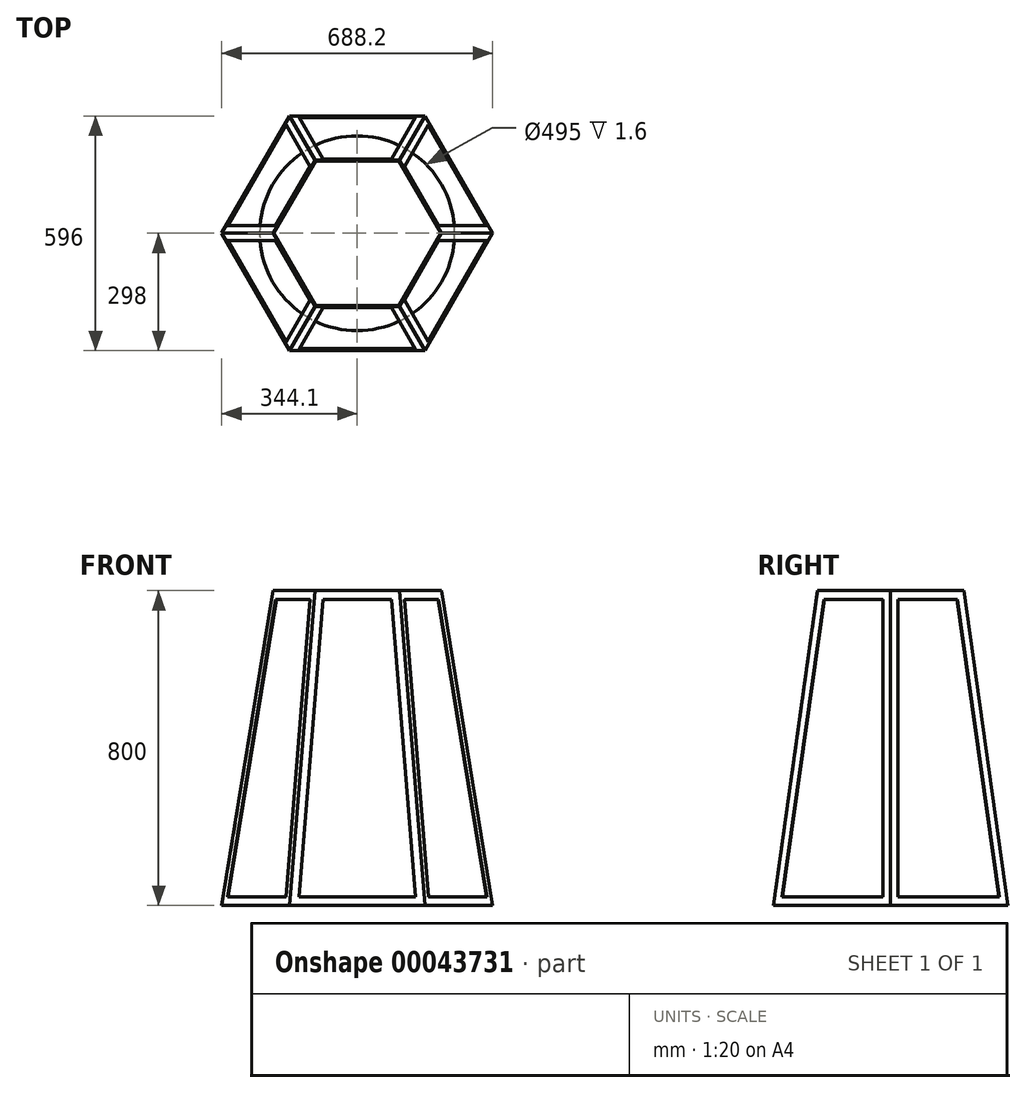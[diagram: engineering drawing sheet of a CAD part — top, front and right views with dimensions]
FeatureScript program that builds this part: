
annotation { "Feature Type Name" : "Feature", "Feature Type Description" : "" }
export const myFeature = defineFeature(function(context is Context, id is Id, definition is map)
    precondition{}
    {
        {
            var Q0;
            Q0=qCreatedBy(makeId("Top.planeOp"),FACE);
            var sketch = newSketch(context, id + "F0", { "sketchPlane" : qUnion([Q0])});
            skCircle(sketch, "E0.cCircle", {"center": v(0, 0) * mm, "radius": 298 * mm, "construction": true});
            skLineSegment(sketch, "E0.0", {"start": v(-172.05, 298) * mm, "end": v(172.05, 298) * mm});
            skLineSegment(sketch, "E0.1", {"start": v(172.05, 298) * mm, "end": v(344.1, 0) * mm});
            skLineSegment(sketch, "E0.2", {"start": v(344.1, 0) * mm, "end": v(172.05, -298) * mm});
            skLineSegment(sketch, "E0.3", {"start": v(172.05, -298) * mm, "end": v(-172.05, -298) * mm});
            skLineSegment(sketch, "E0.4", {"start": v(-172.05, -298) * mm, "end": v(-344.1, 0) * mm});
            skLineSegment(sketch, "E0.5", {"start": v(-344.1, 0) * mm, "end": v(-172.05, 298) * mm});
            skPoint(sketch, "E0.0.midPoint", {"position": v(0, 298) * mm});
            skSolve(sketch);
        }
        {
            var Q0;
            Q0=makeQuery(id+"F0.imprint","IMPRINT",FACE,{"disambiguationData":[TD([[makeQuery(id+"F0.imprint","IMPRINT",EDGE,{"derivedFrom":sQuery(id+"F0.wireOp",EDGE,"E0.0")}),-1.0]])]});
            extrude(context, id + "F1", {"entities" : qUnion([Q0]), "depth" : 800 * mm, "hasDraft" : true, "draftAngle" : 8 * degree, "draftPullDirection" : true});
        }
        {
            var Q0;
            Q0=makeQuery(id+"F1.opExtrude","CAP_FACE",FACE,{"disambiguationData":[OSD([sQuery(id+"F0.wireOp",EDGE,"E0.0"),sQuery(id+"F0.wireOp",EDGE,"E0.1"),sQuery(id+"F0.wireOp",EDGE,"E0.2"),sQuery(id+"F0.wireOp",EDGE,"E0.3"),sQuery(id+"F0.wireOp",EDGE,"E0.4"),sQuery(id+"F0.wireOp",EDGE,"E0.5")])],"isStart":false});
            shell(context, id + "F2", {"entities" : qUnion([Q0]), "thickness" : 1.6 * mm});
        }
        {
            var Q0;
            Q0=makeQuery(id+"F0.imprint","IMPRINT",FACE,{"disambiguationData":[TD([[makeQuery(id+"F0.imprint","IMPRINT",EDGE,{"derivedFrom":sQuery(id+"F0.wireOp",EDGE,"E0.0")}),-1.0]])]});
            var sketch = newSketch(context, id + "F3", { "sketchPlane" : qUnion([Q0])});
            skCircle(sketch, "E1", {"center": v(0, 0) * mm, "radius": 247.5 * mm});
            skSolve(sketch);
        }
        {
            var Q0;
            Q0 = qSketchRegion(id + "F3", true);
            extrude(context, id + "F4", {"entities" : qUnion([Q0]), "operationType" : NewBodyOperationType.REMOVE, "depth" : 25 * mm});
        }
        {
            var Q0;
            Q0=makeQuery(id+"F1.opExtrude","SWEPT_FACE",FACE,{"disambiguationData":[OSD([sQuery(id+"F0.wireOp",EDGE,"E0.3")])]});
            var sketch = newSketch(context, id + "F5", { "sketchPlane" : qUnion([Q0])});
            skLineSegment(sketch, "E2", {"start": v(-172.05, -41.47) * mm, "end": v(-107.14, 766.39) * mm});
            skLineSegment(sketch, "E3", {"start": v(-107.14, 766.39) * mm, "end": v(107.14, 766.39) * mm});
            skLineSegment(sketch, "E4", {"start": v(107.14, 766.39) * mm, "end": v(172.05, -41.47) * mm});
            skLineSegment(sketch, "E5", {"start": v(172.05, -41.47) * mm, "end": v(-172.05, -41.47) * mm});
            skLineSegment(sketch, "E6.0", {"start": v(-148.21, -19.47) * mm, "end": v(148.21, -19.47) * mm});
            skLineSegment(sketch, "E6.1", {"start": v(-86.83, 744.39) * mm, "end": v(-148.21, -19.47) * mm});
            skLineSegment(sketch, "E6.2", {"start": v(86.83, 744.39) * mm, "end": v(-86.83, 744.39) * mm});
            skLineSegment(sketch, "E6.3", {"start": v(148.21, -19.47) * mm, "end": v(86.83, 744.39) * mm});
            skSolve(sketch);
        }
        {
            var Q0;
            Q0=makeQuery(id+"F5.imprint","IMPRINT",FACE,{"disambiguationData":[TD([[makeQuery(id+"F5.imprint","IMPRINT",EDGE,{"derivedFrom":sQuery(id+"F5.wireOp",EDGE,"E6.0")}),1.0]])]});
            extrude(context, id + "F6", {"entities" : qUnion([Q0]), "operationType" : NewBodyOperationType.REMOVE, "oppositeDirection" : true, "depth" : 25 * mm});
        }
        {
            var Q0;
            Q0=makeQuery(id+"F1.opExtrude","SWEPT_FACE",FACE,{"disambiguationData":[OSD([sQuery(id+"F0.wireOp",EDGE,"E0.4")])]});
            var sketch = newSketch(context, id + "F7", { "sketchPlane" : qUnion([Q0])});
            skLineSegment(sketch, "E7", {"start": v(-168.18, -55.12) * mm, "end": v(174.82, -27.56) * mm});
            skLineSegment(sketch, "E8", {"start": v(174.82, -27.56) * mm, "end": v(45.41, 772.5) * mm});
            skLineSegment(sketch, "E9", {"start": v(45.41, 772.5) * mm, "end": v(-168.18, 755.35) * mm});
            skLineSegment(sketch, "E10", {"start": v(-168.18, 755.35) * mm, "end": v(-168.18, -55.12) * mm});
            skLineSegment(sketch, "E11.0", {"start": v(-146.18, -31.28) * mm, "end": v(149.3, -7.54) * mm});
            skLineSegment(sketch, "E11.1", {"start": v(-146.18, 735.04) * mm, "end": v(-146.18, -31.28) * mm});
            skLineSegment(sketch, "E11.2", {"start": v(26.93, 748.95) * mm, "end": v(-146.18, 735.04) * mm});
            skLineSegment(sketch, "E11.3", {"start": v(149.3, -7.54) * mm, "end": v(26.93, 748.95) * mm});
            skSolve(sketch);
        }
        {
            var Q0;
            Q0=makeQuery(id+"F7.imprint","IMPRINT",FACE,{"disambiguationData":[TD([[makeQuery(id+"F7.imprint","IMPRINT",EDGE,{"derivedFrom":sQuery(id+"F7.wireOp",EDGE,"E11.0")}),1.0]])]});
            extrude(context, id + "F8", {"entities" : qUnion([Q0]), "operationType" : NewBodyOperationType.REMOVE, "oppositeDirection" : true, "depth" : 25 * mm});
        }
        {
            var Q0;
            Q0=makeQuery(id+"F1.opExtrude","SWEPT_FACE",FACE,{"disambiguationData":[OSD([sQuery(id+"F0.wireOp",EDGE,"E0.5")])]});
            var sketch = newSketch(context, id + "F9", { "sketchPlane" : qUnion([Q0])});
            skLineSegment(sketch, "E12", {"start": v(-45.41, 772.5) * mm, "end": v(168.18, 755.35) * mm});
            skLineSegment(sketch, "E13", {"start": v(168.18, 755.35) * mm, "end": v(168.18, -55.12) * mm});
            skLineSegment(sketch, "E14", {"start": v(168.18, -55.12) * mm, "end": v(-174.82, -27.56) * mm});
            skLineSegment(sketch, "E15", {"start": v(-174.82, -27.56) * mm, "end": v(-45.41, 772.5) * mm});
            skLineSegment(sketch, "E16.0", {"start": v(-26.93, 748.95) * mm, "end": v(146.18, 735.04) * mm});
            skLineSegment(sketch, "E16.1", {"start": v(-149.3, -7.54) * mm, "end": v(-26.93, 748.95) * mm});
            skLineSegment(sketch, "E16.2", {"start": v(146.18, -31.28) * mm, "end": v(-149.3, -7.54) * mm});
            skLineSegment(sketch, "E16.3", {"start": v(146.18, 735.04) * mm, "end": v(146.18, -31.28) * mm});
            skSolve(sketch);
        }
        {
            var Q0;
            Q0=makeQuery(id+"F9.imprint","IMPRINT",FACE,{"disambiguationData":[TD([[makeQuery(id+"F9.imprint","IMPRINT",EDGE,{"derivedFrom":sQuery(id+"F9.wireOp",EDGE,"E16.0")}),-1.0]])]});
            extrude(context, id + "F10", {"entities" : qUnion([Q0]), "operationType" : NewBodyOperationType.REMOVE, "oppositeDirection" : true, "depth" : 25 * mm});
        }
        {
            var Q0;
            Q0=makeQuery(id+"F1.opExtrude","SWEPT_FACE",FACE,{"disambiguationData":[OSD([sQuery(id+"F0.wireOp",EDGE,"E0.0")])]});
            var sketch = newSketch(context, id + "F11", { "sketchPlane" : qUnion([Q0])});
            skLineSegment(sketch, "E17", {"start": v(-172.05, -41.47) * mm, "end": v(-107.14, 766.39) * mm});
            skLineSegment(sketch, "E18", {"start": v(-107.14, 766.39) * mm, "end": v(107.14, 766.39) * mm});
            skLineSegment(sketch, "E19", {"start": v(107.14, 766.39) * mm, "end": v(172.05, -41.47) * mm});
            skLineSegment(sketch, "E20", {"start": v(172.05, -41.47) * mm, "end": v(-172.05, -41.47) * mm});
            skLineSegment(sketch, "E21.0", {"start": v(148.21, -19.47) * mm, "end": v(-148.21, -19.47) * mm});
            skLineSegment(sketch, "E21.1", {"start": v(86.83, 744.39) * mm, "end": v(148.21, -19.47) * mm});
            skLineSegment(sketch, "E21.2", {"start": v(-86.83, 744.39) * mm, "end": v(86.83, 744.39) * mm});
            skLineSegment(sketch, "E21.3", {"start": v(-148.21, -19.47) * mm, "end": v(-86.83, 744.39) * mm});
            skSolve(sketch);
        }
        {
            var Q0;
            Q0=makeQuery(id+"F11.imprint","IMPRINT",FACE,{"disambiguationData":[TD([[makeQuery(id+"F11.imprint","IMPRINT",EDGE,{"derivedFrom":sQuery(id+"F11.wireOp",EDGE,"E21.0")}),-1.0]])]});
            extrude(context, id + "F12", {"entities" : qUnion([Q0]), "operationType" : NewBodyOperationType.REMOVE, "oppositeDirection" : true, "depth" : 25 * mm});
        }
        {
            var Q0;
            Q0=makeQuery(id+"F1.opExtrude","SWEPT_FACE",FACE,{"disambiguationData":[OSD([sQuery(id+"F0.wireOp",EDGE,"E0.1")])]});
            var sketch = newSketch(context, id + "F13", { "sketchPlane" : qUnion([Q0])});
            skLineSegment(sketch, "E22", {"start": v(-168.18, -55.12) * mm, "end": v(174.82, -27.56) * mm});
            skLineSegment(sketch, "E23", {"start": v(174.82, -27.56) * mm, "end": v(45.41, 772.5) * mm});
            skLineSegment(sketch, "E24", {"start": v(45.41, 772.5) * mm, "end": v(-168.18, 755.35) * mm});
            skLineSegment(sketch, "E25", {"start": v(-168.18, 755.35) * mm, "end": v(-168.18, -55.12) * mm});
            skLineSegment(sketch, "E26.0", {"start": v(-146.18, 735.04) * mm, "end": v(-146.18, -31.28) * mm});
            skLineSegment(sketch, "E26.1", {"start": v(26.93, 748.95) * mm, "end": v(-146.18, 735.04) * mm});
            skLineSegment(sketch, "E26.2", {"start": v(149.3, -7.54) * mm, "end": v(26.93, 748.95) * mm});
            skLineSegment(sketch, "E26.3", {"start": v(-146.18, -31.28) * mm, "end": v(149.3, -7.54) * mm});
            skSolve(sketch);
        }
        {
            var Q0;
            Q0=makeQuery(id+"F13.imprint","IMPRINT",FACE,{"disambiguationData":[TD([[makeQuery(id+"F13.imprint","IMPRINT",EDGE,{"derivedFrom":sQuery(id+"F13.wireOp",EDGE,"E26.0")}),1.0]])]});
            extrude(context, id + "F14", {"entities" : qUnion([Q0]), "operationType" : NewBodyOperationType.REMOVE, "oppositeDirection" : true, "depth" : 25 * mm});
        }
        {
            var Q0;
            Q0=makeQuery(id+"F1.opExtrude","SWEPT_FACE",FACE,{"disambiguationData":[OSD([sQuery(id+"F0.wireOp",EDGE,"E0.2")])]});
            var sketch = newSketch(context, id + "F15", { "sketchPlane" : qUnion([Q0])});
            skLineSegment(sketch, "E27", {"start": v(-174.82, -27.56) * mm, "end": v(168.18, -55.12) * mm});
            skLineSegment(sketch, "E28", {"start": v(168.18, -55.12) * mm, "end": v(168.18, 755.35) * mm});
            skLineSegment(sketch, "E29", {"start": v(168.18, 755.35) * mm, "end": v(-45.41, 772.5) * mm});
            skLineSegment(sketch, "E30", {"start": v(-45.41, 772.5) * mm, "end": v(-174.82, -27.56) * mm});
            skLineSegment(sketch, "E31.0", {"start": v(-149.3, -7.54) * mm, "end": v(146.18, -31.28) * mm});
            skLineSegment(sketch, "E31.1", {"start": v(-26.93, 748.95) * mm, "end": v(-149.3, -7.54) * mm});
            skLineSegment(sketch, "E31.2", {"start": v(146.18, 735.04) * mm, "end": v(-26.93, 748.95) * mm});
            skLineSegment(sketch, "E31.3", {"start": v(146.18, -31.28) * mm, "end": v(146.18, 735.04) * mm});
            skSolve(sketch);
        }
        {
            var Q0;
            Q0=makeQuery(id+"F15.imprint","IMPRINT",FACE,{"disambiguationData":[TD([[makeQuery(id+"F15.imprint","IMPRINT",EDGE,{"derivedFrom":sQuery(id+"F15.wireOp",EDGE,"E31.0")}),1.0]])]});
            extrude(context, id + "F16", {"entities" : qUnion([Q0]), "operationType" : NewBodyOperationType.REMOVE, "oppositeDirection" : true, "depth" : 25 * mm});
        }
    });
